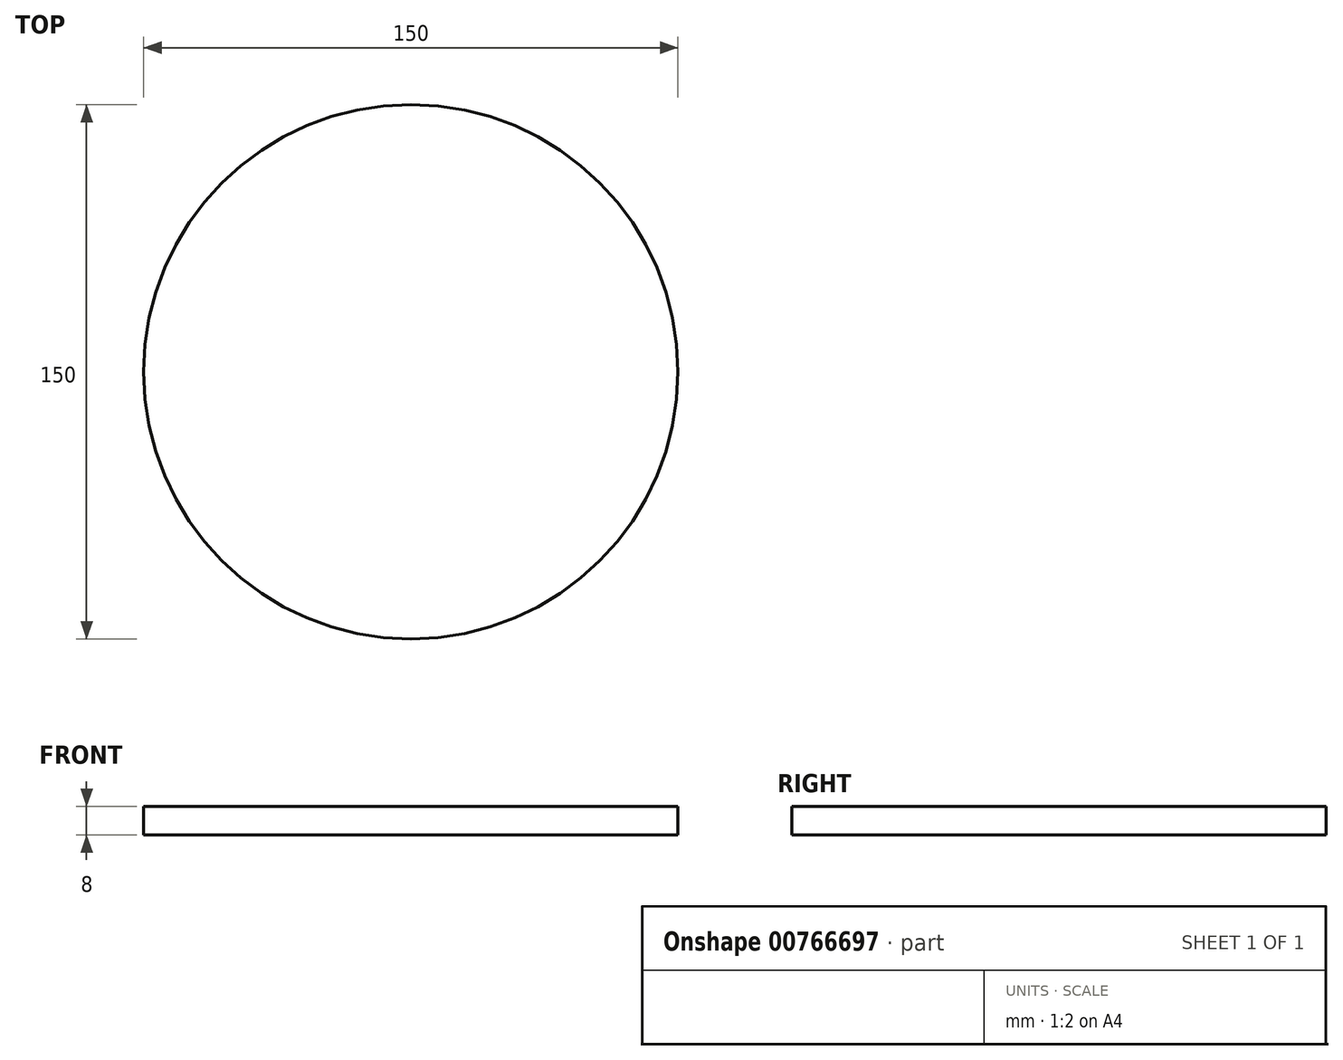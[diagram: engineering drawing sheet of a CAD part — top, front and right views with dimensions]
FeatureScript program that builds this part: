
annotation { "Feature Type Name" : "Feature", "Feature Type Description" : "" }
export const myFeature = defineFeature(function(context is Context, id is Id, definition is map)
    precondition{}
    {
        {
            var Q0;
            Q0=qCreatedBy(makeId("Top.planeOp"),FACE);
            var sketch = newSketch(context, id + "F0", { "sketchPlane" : qUnion([Q0])});
            skCircle(sketch, "E0", {"center": v(0, 0) * mm, "radius": 75 * mm});
            skSolve(sketch);
        }
        {
            var Q0;
            Q0=makeQuery(id+"F0.imprint","IMPRINT",FACE,{"disambiguationData":[TD([[makeQuery(id+"F0.imprint","IMPRINT",EDGE,{"derivedFrom":sQuery(id+"F0.wireOp",EDGE,"E0")}),1.0]])]});
            extrude(context, id + "F1", {"entities" : qUnion([Q0]), "depth" : 8 * mm, "offsetDistance" : 25 * mm});
        }
    });
